# Revit family: Cortadora_CA-41_1_GENERADO
name_source: partatom
category: Equipos especializados
units: mm (PartAtom-declared; Revit-internal decimal feet)

## family parameters
Compartido = No
Corte con vacíos al cargar = No
Cota de conector redondo = Diámetro de uso
Número OmniClass = 23.21.21.31.19.11
Punto de cálculo de habitación = No
Se basa en plano de trabajo = No
Siempre vertical = Sí
Tipo de pieza = Normal

## types (8) — shared parameters
Depth = 396 mm  [stored 1.29921 ft]
Fabricante = SAMMIC S.L.
Foodservice Equipment Identifier = Sí
HP = 0.74
Height = 652 mm  [stored 2.13911 ft]
Revision Code = 1
Specification by Manufacturer = Single-speed motor block +  large production attachment.
URL = https://www.sammic.com
URL Cutsheet = http://www.sammic.com
Watts = 550 W
Width = 391 mm  [stored 1.28281 ft]
zero-valued in all types: Elevación por defecto

## per-type parameters (varying)
| type | Comentarios de tipo | Conn Plug | Cycle | Electric Connection Type | FL Amps | Modelo | Phase | Volts | Weight in Pounds |
| Vegetable preparation machine CA-41 230-400/50/3N | High production vegetable preparation machine with an hourly output of up to 1300 lbs. / 650 Kg.

ELECTRICAL DATA:

230V/50Hz/3~ (2.6A) |  | 50 Hz | 3P+N+G | 2 A | 1050721 | 3 | 400 V | 51.8 |
| Vegetable preparation machine CA-41 230/50/1 | High production vegetable preparation machine with an hourly output of up to 1300 lbs. / 650 Kg. | EU (SCHUKO 2P+G) | 50 Hz |  | 4 A | 1050719 | 1 | 230 V | 52.9 |
| Vegetable preparation machine CA-41 120/60/1 | High production vegetable preparation machine with an hourly output of up to 1300 lbs. / 650 Kg. | USA (NEMA 5-15P / 2P+G) | 60 Hz |  | 4 A | 1050720 | 1 | 120 V | 52.9 |
| Vegetable preparation machines CA-41 220/60/1 KSA | High production vegetable preparation machine with an hourly output of up to 1300 lbs. / 650 Kg. | UK (BS 1363 13A / 2P+G) | 60 Hz | 2P+G | 4 A | 1050722 | 1 | 220 V | 52.9 |
| Vegetable preparation machine CA-41 220/60/1 | High production vegetable preparation machine with an hourly output of up to 1300 lbs. / 650 Kg. | EU (SCHUKO 2P+G) | 60 Hz |  | 4 A | 1050725 | 1 | 220 V | 52.9 |
| Vegetable preparation machine CA-41 220-380/60/3N | High production vegetable preparation machine with an hourly output of up to 1300 lbs. / 650 Kg.

ELECTRICAL DATA:

380V/60Hz/3N~ (1.5A) |  | 60 Hz | 3P+G | 3 A | 1050726 | 3 | 220 V | 51.8 |
| Vegetable preparation machine CA-41 230/50/1 AUS | High production vegetable preparation machine with an hourly output of up to 1300 lbs. / 650 Kg. | AU/NZ (AS 3112 10A / 2P) | 50 Hz |  | 4 A | 1050728 | 1 | 230 V | 52.9 |
| Vegetable preparation machine CA-41 230/50/1 UK | High production vegetable preparation machine with an hourly output of up to 1300 lbs. / 650 Kg. | UK (BS 1363 13A / 2P+G) | 50 Hz |  | 4 A | 1050731 | 1 | 230 V | 52.9 |

note: column(s) folded — value = type name in every type: Descripción

note: [stored X ft] marks values corroborated as IEEE doubles in the binary element streams (Revit-internal decimal feet)
